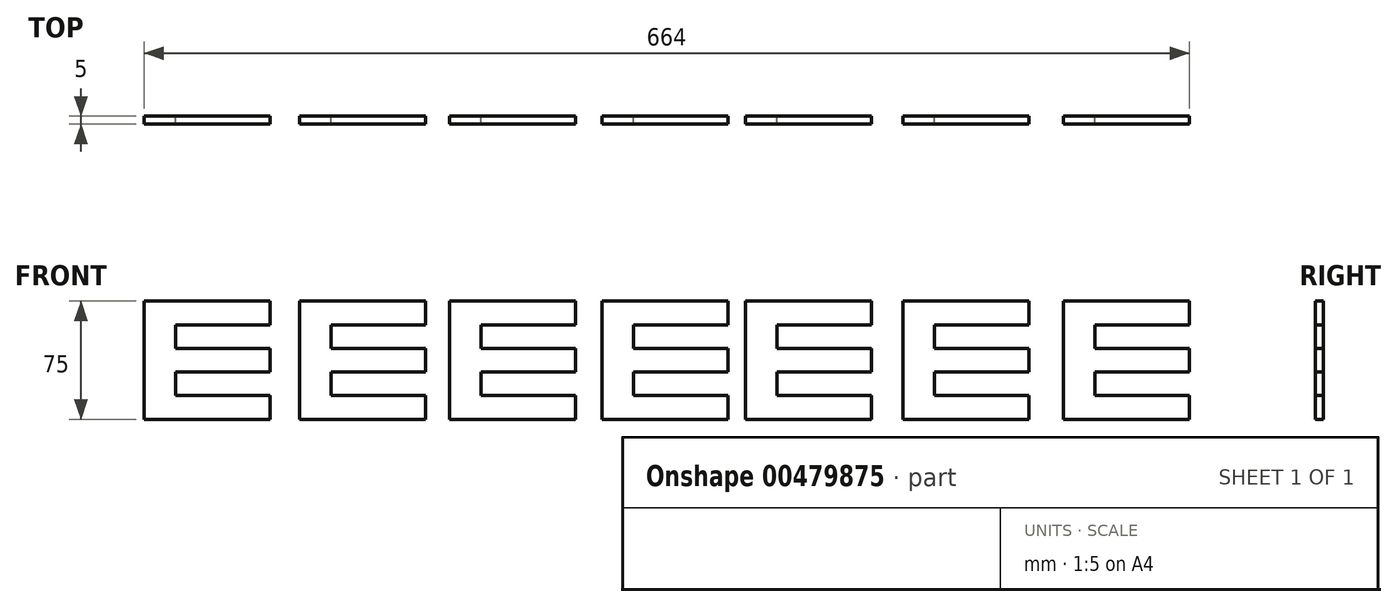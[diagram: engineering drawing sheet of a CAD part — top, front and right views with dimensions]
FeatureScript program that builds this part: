
annotation { "Feature Type Name" : "Feature", "Feature Type Description" : "" }
export const myFeature = defineFeature(function(context is Context, id is Id, definition is map)
    precondition{}
    {
        {
            var Q0;
            Q0=qCreatedBy(makeId("Front.planeOp"),FACE);
            var sketch = newSketch(context, id + "F0", { "sketchPlane" : qUnion([Q0])});
            skLineSegment(sketch, "E0.bottom", {"start": v(-47.5, 37.5) * mm, "end": v(32.5, 37.5) * mm});
            skLineSegment(sketch, "E0.top", {"start": v(-47.5, -37.5) * mm, "end": v(32.5, -37.5) * mm});
            skLineSegment(sketch, "E0.right", {"start": v(32.5, 37.5) * mm, "end": v(32.5, 22.5) * mm});
            skLineSegment(sketch, "E1", {"start": v(-27.5, 22.5) * mm, "end": v(-27.5, 7.5) * mm});
            skLineSegment(sketch, "E2", {"start": v(-27.5, 22.5) * mm, "end": v(32.5, 22.5) * mm});
            skLineSegment(sketch, "E3", {"start": v(-27.5, 7.5) * mm, "end": v(32.5, 7.5) * mm});
            skLineSegment(sketch, "E4", {"start": v(-27.5, -7.5) * mm, "end": v(32.5, -7.5) * mm});
            skLineSegment(sketch, "E5", {"start": v(-27.5, -22.5) * mm, "end": v(32.5, -22.5) * mm});
            skLineSegment(sketch, "E6.trimOffspring", {"start": v(-27.5, -7.5) * mm, "end": v(-27.5, -22.5) * mm});
            skLineSegment(sketch, "E7.trimOffspring", {"start": v(32.5, 7.5) * mm, "end": v(32.5, -7.5) * mm});
            skLineSegment(sketch, "E8.trimOffspring", {"start": v(32.5, -22.5) * mm, "end": v(32.5, -37.5) * mm});
            skLineSegment(sketch, "E9", {"start": v(-47.5, 37.5) * mm, "end": v(-47.5, -37.5) * mm});
            skSolve(sketch);
        }
        {
            var Q0;
            Q0 = qSketchRegion(id + "F0", true);
            extrude(context, id + "F1", {"entities" : qUnion([Q0]), "depth" : 5 * mm});
        }
        {
            var Q0;
            Q0=makeQuery(id+"F1.opExtrude","SWEPT_BODY",BODY,{"disambiguationData":[OSD([sQuery(id+"F0.wireOp",EDGE,"E0.bottom"),sQuery(id+"F0.wireOp",EDGE,"E0.top"),sQuery(id+"F0.wireOp",EDGE,"E0.right"),sQuery(id+"F0.wireOp",EDGE,"E1"),sQuery(id+"F0.wireOp",EDGE,"E2"),sQuery(id+"F0.wireOp",EDGE,"E3"),sQuery(id+"F0.wireOp",EDGE,"E4"),sQuery(id+"F0.wireOp",EDGE,"E5"),sQuery(id+"F0.wireOp",EDGE,"E6.trimOffspring"),sQuery(id+"F0.wireOp",EDGE,"E7.trimOffspring"),sQuery(id+"F0.wireOp",EDGE,"E8.trimOffspring"),sQuery(id+"F0.wireOp",EDGE,"E9")])]});
            transform(context, id + "F2", {"entities" : qUnion([Q0]), "transformType" : TransformType.TRANSLATION_3D, "dx" : -95 * mm, "dy" : 0 * mm, "dz" : 0 * mm, "makeCopy" : true});
        }
        {
            var Q0;
            Q0=makeQuery(id+"F2.opPattern","COPY",BODY,{"derivedFrom":makeQuery(id+"F1.opExtrude","SWEPT_BODY",BODY,{"disambiguationData":[OSD([sQuery(id+"F0.wireOp",EDGE,"E0.bottom"),sQuery(id+"F0.wireOp",EDGE,"E0.top"),sQuery(id+"F0.wireOp",EDGE,"E0.right"),sQuery(id+"F0.wireOp",EDGE,"E1"),sQuery(id+"F0.wireOp",EDGE,"E2"),sQuery(id+"F0.wireOp",EDGE,"E3"),sQuery(id+"F0.wireOp",EDGE,"E4"),sQuery(id+"F0.wireOp",EDGE,"E5"),sQuery(id+"F0.wireOp",EDGE,"E6.trimOffspring"),sQuery(id+"F0.wireOp",EDGE,"E7.trimOffspring"),sQuery(id+"F0.wireOp",EDGE,"E8.trimOffspring"),sQuery(id+"F0.wireOp",EDGE,"E9")])]}),"instanceName":"1"});
            transform(context, id + "F3", {"entities" : qUnion([Q0]), "transformType" : TransformType.TRANSLATION_3D, "dx" : -99 * mm, "dy" : 0 * mm, "dz" : 0 * mm, "makeCopy" : true});
        }
        {
            var Q0;
            Q0=makeQuery(id+"F1.opExtrude","SWEPT_BODY",BODY,{"disambiguationData":[OSD([sQuery(id+"F0.wireOp",EDGE,"E0.bottom"),sQuery(id+"F0.wireOp",EDGE,"E0.top"),sQuery(id+"F0.wireOp",EDGE,"E0.right"),sQuery(id+"F0.wireOp",EDGE,"E1"),sQuery(id+"F0.wireOp",EDGE,"E2"),sQuery(id+"F0.wireOp",EDGE,"E3"),sQuery(id+"F0.wireOp",EDGE,"E4"),sQuery(id+"F0.wireOp",EDGE,"E5"),sQuery(id+"F0.wireOp",EDGE,"E6.trimOffspring"),sQuery(id+"F0.wireOp",EDGE,"E7.trimOffspring"),sQuery(id+"F0.wireOp",EDGE,"E8.trimOffspring"),sQuery(id+"F0.wireOp",EDGE,"E9")])]});
            transform(context, id + "F4", {"entities" : qUnion([Q0]), "transformType" : TransformType.TRANSLATION_3D, "dx" : 97 * mm, "dy" : 0 * mm, "dz" : 0 * mm, "makeCopy" : true});
        }
        {
            var Q0;
            Q0=makeQuery(id+"F4.opPattern","COPY",BODY,{"derivedFrom":makeQuery(id+"F1.opExtrude","SWEPT_BODY",BODY,{"disambiguationData":[OSD([sQuery(id+"F0.wireOp",EDGE,"E0.bottom"),sQuery(id+"F0.wireOp",EDGE,"E0.top"),sQuery(id+"F0.wireOp",EDGE,"E0.right"),sQuery(id+"F0.wireOp",EDGE,"E1"),sQuery(id+"F0.wireOp",EDGE,"E2"),sQuery(id+"F0.wireOp",EDGE,"E3"),sQuery(id+"F0.wireOp",EDGE,"E4"),sQuery(id+"F0.wireOp",EDGE,"E5"),sQuery(id+"F0.wireOp",EDGE,"E6.trimOffspring"),sQuery(id+"F0.wireOp",EDGE,"E7.trimOffspring"),sQuery(id+"F0.wireOp",EDGE,"E8.trimOffspring"),sQuery(id+"F0.wireOp",EDGE,"E9")])]}),"instanceName":"1"});
            transform(context, id + "F5", {"entities" : qUnion([Q0]), "transformType" : TransformType.TRANSLATION_3D, "dx" : 91 * mm, "dy" : 0 * mm, "dz" : 0 * mm, "makeCopy" : true});
        }
        {
            var Q0;
            Q0=makeQuery(id+"F5.opPattern","COPY",BODY,{"derivedFrom":makeQuery(id+"F4.opPattern","COPY",BODY,{"derivedFrom":makeQuery(id+"F1.opExtrude","SWEPT_BODY",BODY,{"disambiguationData":[OSD([sQuery(id+"F0.wireOp",EDGE,"E0.bottom"),sQuery(id+"F0.wireOp",EDGE,"E0.top"),sQuery(id+"F0.wireOp",EDGE,"E0.right"),sQuery(id+"F0.wireOp",EDGE,"E1"),sQuery(id+"F0.wireOp",EDGE,"E2"),sQuery(id+"F0.wireOp",EDGE,"E3"),sQuery(id+"F0.wireOp",EDGE,"E4"),sQuery(id+"F0.wireOp",EDGE,"E5"),sQuery(id+"F0.wireOp",EDGE,"E6.trimOffspring"),sQuery(id+"F0.wireOp",EDGE,"E7.trimOffspring"),sQuery(id+"F0.wireOp",EDGE,"E8.trimOffspring"),sQuery(id+"F0.wireOp",EDGE,"E9")])]}),"instanceName":"1"}),"instanceName":"1"});
            transform(context, id + "F6", {"entities" : qUnion([Q0]), "transformType" : TransformType.TRANSLATION_3D, "dx" : 100 * mm, "dy" : 0 * mm, "dz" : 0 * mm, "makeCopy" : true});
        }
        {
            var Q0;
            Q0=makeQuery(id+"F6.opPattern","COPY",BODY,{"derivedFrom":makeQuery(id+"F5.opPattern","COPY",BODY,{"derivedFrom":makeQuery(id+"F4.opPattern","COPY",BODY,{"derivedFrom":makeQuery(id+"F1.opExtrude","SWEPT_BODY",BODY,{"disambiguationData":[OSD([sQuery(id+"F0.wireOp",EDGE,"E0.bottom"),sQuery(id+"F0.wireOp",EDGE,"E0.top"),sQuery(id+"F0.wireOp",EDGE,"E0.right"),sQuery(id+"F0.wireOp",EDGE,"E1"),sQuery(id+"F0.wireOp",EDGE,"E2"),sQuery(id+"F0.wireOp",EDGE,"E3"),sQuery(id+"F0.wireOp",EDGE,"E4"),sQuery(id+"F0.wireOp",EDGE,"E5"),sQuery(id+"F0.wireOp",EDGE,"E6.trimOffspring"),sQuery(id+"F0.wireOp",EDGE,"E7.trimOffspring"),sQuery(id+"F0.wireOp",EDGE,"E8.trimOffspring"),sQuery(id+"F0.wireOp",EDGE,"E9")])]}),"instanceName":"1"}),"instanceName":"1"}),"instanceName":"1"});
            transform(context, id + "F7", {"entities" : qUnion([Q0]), "transformType" : TransformType.TRANSLATION_3D, "dx" : 102 * mm, "dy" : 0 * mm, "dz" : 0 * mm, "makeCopy" : true});
        }
    });
